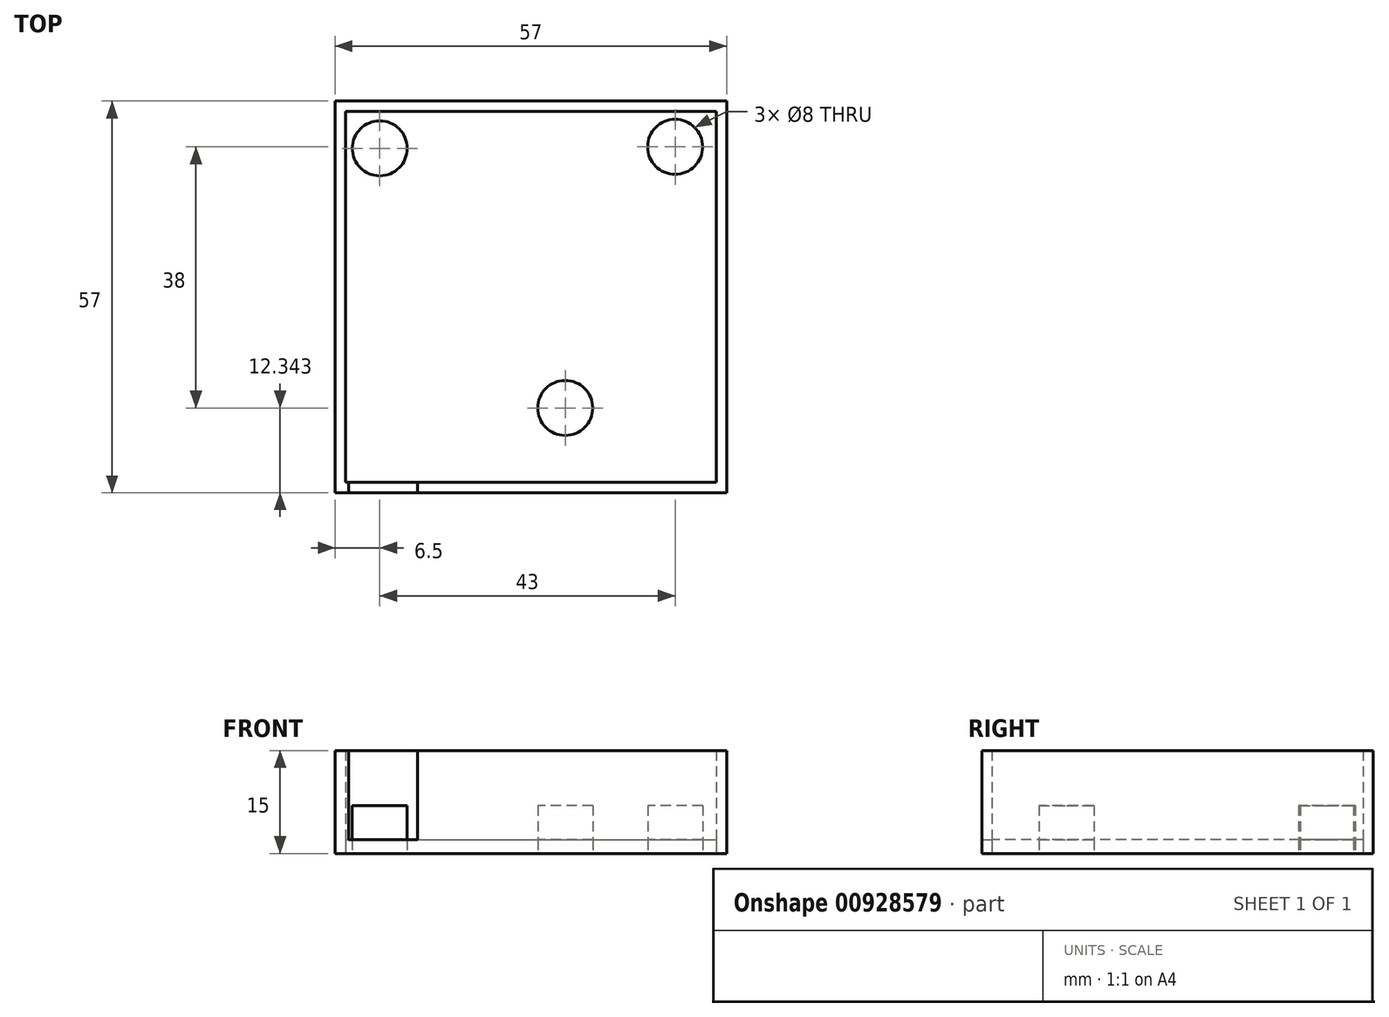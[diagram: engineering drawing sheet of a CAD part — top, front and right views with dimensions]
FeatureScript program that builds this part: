
annotation { "Feature Type Name" : "Feature", "Feature Type Description" : "" }
export const myFeature = defineFeature(function(context is Context, id is Id, definition is map)
    precondition{}
    {
        {
            var Q0;
            Q0=qCreatedBy(makeId("Top.planeOp"),FACE);
            var sketch = newSketch(context, id + "F0", { "sketchPlane" : qUnion([Q0])});
            skLineSegment(sketch, "E0.bottom", {"start": v(-28.5, 28.5) * mm, "end": v(28.5, 28.5) * mm});
            skLineSegment(sketch, "E0.top", {"start": v(-28.5, -28.5) * mm, "end": v(28.5, -28.5) * mm});
            skLineSegment(sketch, "E0.left", {"start": v(-28.5, 28.5) * mm, "end": v(-28.5, -28.5) * mm});
            skLineSegment(sketch, "E0.right", {"start": v(28.5, 28.5) * mm, "end": v(28.5, -28.5) * mm});
            skPoint(sketch, "E0.middle", {"position": v(0, 0) * mm});
            skCircle(sketch, "E1", {"center": v(-22, 21.62) * mm, "radius": 4 * mm});
            skCircle(sketch, "E2", {"center": v(21, 21.84) * mm, "radius": 4 * mm});
            skCircle(sketch, "E3", {"center": v(5, -16.16) * mm, "radius": 4 * mm});
            skLineSegment(sketch, "E4.bottom", {"start": v(-27, 27) * mm, "end": v(27, 27) * mm});
            skLineSegment(sketch, "E4.top", {"start": v(-27, -27) * mm, "end": v(27, -27) * mm});
            skLineSegment(sketch, "E4.left", {"start": v(-27, 27) * mm, "end": v(-27, -27) * mm});
            skLineSegment(sketch, "E4.right", {"start": v(27, 27) * mm, "end": v(27, -27) * mm});
            skSolve(sketch);
        }
        {
            var Q0;
            Q0=makeQuery(id+"F0.imprint","IMPRINT",FACE,{"disambiguationData":[TD([[makeQuery(id+"F0.imprint","IMPRINT",EDGE,{"derivedFrom":sQuery(id+"F0.wireOp",EDGE,"E0.bottom")}),-1.0]])]});
            extrude(context, id + "F1", {"entities" : qUnion([Q0]), "depth" : 15 * mm, "offsetDistance" : 25 * mm});
        }
        {
            var Q0;
            Q0=makeQuery(id+"F0.imprint","IMPRINT",FACE,{"disambiguationData":[TD([[makeQuery(id+"F0.imprint","IMPRINT",EDGE,{"derivedFrom":sQuery(id+"F0.wireOp",EDGE,"E1")}),1.0]])]});
            var Q1;
            Q1=makeQuery(id+"F0.imprint","IMPRINT",FACE,{"disambiguationData":[TD([[makeQuery(id+"F0.imprint","IMPRINT",EDGE,{"derivedFrom":sQuery(id+"F0.wireOp",EDGE,"E2")}),1.0]])]});
            var Q2;
            Q2=makeQuery(id+"F0.imprint","IMPRINT",FACE,{"disambiguationData":[TD([[makeQuery(id+"F0.imprint","IMPRINT",EDGE,{"derivedFrom":sQuery(id+"F0.wireOp",EDGE,"E3")}),1.0]])]});
            extrude(context, id + "F2", {"entities" : qUnion([Q0, Q1, Q2]), "operationType" : NewBodyOperationType.ADD, "depth" : 7 * mm, "offsetDistance" : 25 * mm});
        }
        {
            var Q0;
            Q0=makeQuery(id+"F0.imprint","IMPRINT",FACE,{"disambiguationData":[TD([[makeQuery(id+"F0.imprint","IMPRINT",EDGE,{"derivedFrom":sQuery(id+"F0.wireOp",EDGE,"E1")}),-1.0]])]});
            extrude(context, id + "F3", {"entities" : qUnion([Q0]), "depth" : 2 * mm, "offsetDistance" : 25 * mm});
        }
        {
            var Q0;
            Q0=qCreatedBy(makeId("Front.planeOp"),FACE);
            var sketch = newSketch(context, id + "F4", { "sketchPlane" : qUnion([Q0])});
            skLineSegment(sketch, "E5.bottom", {"start": v(-26.5, 16) * mm, "end": v(-16.5, 16) * mm});
            skLineSegment(sketch, "E5.top", {"start": v(-26.5, 2) * mm, "end": v(-16.5, 2) * mm});
            skLineSegment(sketch, "E5.left", {"start": v(-26.5, 16) * mm, "end": v(-26.5, 2) * mm});
            skLineSegment(sketch, "E5.right", {"start": v(-16.5, 16) * mm, "end": v(-16.5, 2) * mm});
            skSolve(sketch);
        }
        {
            var Q0;
            Q0 = qSketchRegion(id + "F4", true);
            var Q1;
            Q1=makeQuery(id+"F1.opExtrude","SWEPT_FACE",FACE,{"disambiguationData":[OSD([sQuery(id+"F0.wireOp",EDGE,"E0.top")])]});
            extrude(context, id + "F5", {"entities" : qUnion([Q0, Q1]), "operationType" : NewBodyOperationType.REMOVE, "endBound" : BoundingType.THROUGH_ALL, "depth" : 25 * mm, "offsetDistance" : 25 * mm});
        }
    });
